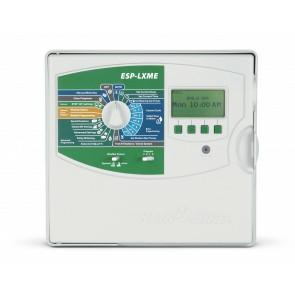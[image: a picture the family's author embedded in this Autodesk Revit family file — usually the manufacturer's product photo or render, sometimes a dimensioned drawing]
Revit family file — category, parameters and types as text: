
# Revit family: Controller ESP-LXME
name_source: partatom
category: Dispositivos de dados
units: mm (PartAtom-declared; Revit-internal decimal feet)

## family parameters
Com base no plano de trabalho = Não
Compartilhado = Não
Corte com vazios quando carregada = Não
Cota do conector redondo = Utilizar diâmetro
Manter orientação da anotação = Não
Número OmniClass = 23.85.50.00
Ponto de cálculo do ambiente = Não
Sempre na vertical = Sim
Tipo de parte = Normal
Título OmniClass = Communication Systems

## types (8) — shared parameters
Corrente de Saída = 2 A
DTT2 = 120  [stored 0.393701 ft]
Depth = 130
Height from base = 800  [stored 2.62467 ft]
Heigth = 322  [stored 1.05643 ft]
Power = 30 VA
RainBird: Code = F42230
RainBird: Product Link = www.rainbird.com
Supply = 120 VA
SupportProjetos: Level of Detail = LOD 300
SupportProjetos: Review = R00
Tipo de imagem = esp-lxme_no_cover_straight_cc.jpg
URL = www.rainbird.com
Width = 364  [stored 1.19423 ft]
zero-valued in all types: Elevação padrão

## type names (no varying parameters)
- ESP8LXME
- IESP8LXME
- ESP12LXMEF
- I12LXMEF
- ESPLXMSM12
- ESPLXMSM8
- FSMLXME
- LXBASEMOD

note: column(s) folded — value = type name in every type: Modelo, RainBird: Description

note: [stored X ft] marks values corroborated as IEEE doubles in the binary element streams (Revit-internal decimal feet)
